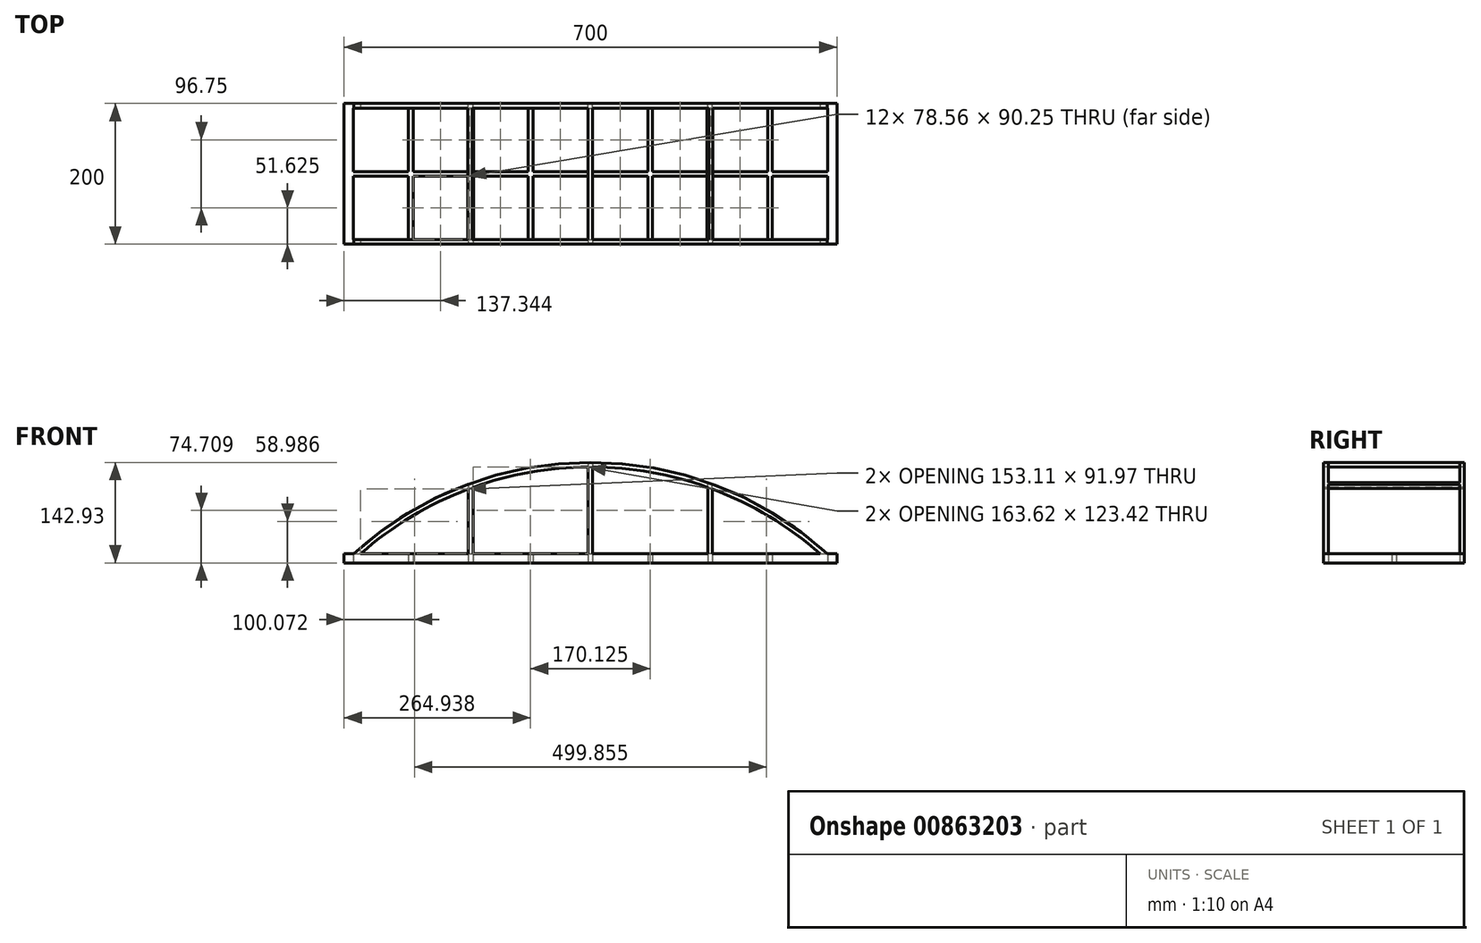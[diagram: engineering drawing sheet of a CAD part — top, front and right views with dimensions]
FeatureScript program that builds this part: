
annotation { "Feature Type Name" : "Feature", "Feature Type Description" : "" }
export const myFeature = defineFeature(function(context is Context, id is Id, definition is map)
    precondition{}
    {
        {
            var Q0;
            Q0=qCreatedBy(makeId("Top.planeOp"),FACE);
            var sketch = newSketch(context, id + "F0", { "sketchPlane" : qUnion([Q0])});
            skLineSegment(sketch, "E0.bottom", {"start": v(-350, 100) * mm, "end": v(350, 100) * mm});
            skLineSegment(sketch, "E0.top", {"start": v(-350, -100) * mm, "end": v(350, -100) * mm});
            skLineSegment(sketch, "E0.left", {"start": v(-350, 100) * mm, "end": v(-350, -100) * mm});
            skLineSegment(sketch, "E0.right", {"start": v(350, 100) * mm, "end": v(350, -100) * mm});
            skLineSegment(sketch, "E1.bottom", {"start": v(-337, 93.5) * mm, "end": v(337, 93.5) * mm});
            skLineSegment(sketch, "E1.top", {"start": v(-337, -93.5) * mm, "end": v(337, -93.5) * mm});
            skLineSegment(sketch, "E1.left", {"start": v(-337, 93.5) * mm, "end": v(-337, -93.5) * mm});
            skLineSegment(sketch, "E1.right", {"start": v(337, 93.5) * mm, "end": v(337, -93.5) * mm});
            skLineSegment(sketch, "E2.bottom", {"start": v(-337, 3.25) * mm, "end": v(337, 3.25) * mm});
            skLineSegment(sketch, "E2.top", {"start": v(-337, -3.25) * mm, "end": v(337, -3.25) * mm});
            skLineSegment(sketch, "E2.left", {"start": v(-337, 3.25) * mm, "end": v(-337, -3.25) * mm});
            skLineSegment(sketch, "E2.right", {"start": v(337, 3.25) * mm, "end": v(337, -3.25) * mm});
            skLineSegment(sketch, "E3.bottom", {"start": v(-258.44, 93.5) * mm, "end": v(-251.94, 93.5) * mm});
            skLineSegment(sketch, "E3.top", {"start": v(-258.44, -93.5) * mm, "end": v(-251.94, -93.5) * mm});
            skLineSegment(sketch, "E3.left", {"start": v(-258.44, 93.5) * mm, "end": v(-258.44, -93.5) * mm});
            skLineSegment(sketch, "E3.right", {"start": v(-251.94, 93.5) * mm, "end": v(-251.94, -93.5) * mm});
            skLineSegment(sketch, "E4.bottom", {"start": v(-173.38, 93.5) * mm, "end": v(-166.88, 93.5) * mm});
            skLineSegment(sketch, "E4.top", {"start": v(-173.37, -93.5) * mm, "end": v(-166.87, -93.5) * mm});
            skLineSegment(sketch, "E4.left", {"start": v(-173.38, 93.5) * mm, "end": v(-173.37, -93.5) * mm});
            skLineSegment(sketch, "E4.right", {"start": v(-166.88, 93.5) * mm, "end": v(-166.87, -93.5) * mm});
            skLineSegment(sketch, "E5.bottom", {"start": v(-88.31, 93.5) * mm, "end": v(-81.81, 93.5) * mm});
            skLineSegment(sketch, "E5.top", {"start": v(-88.31, -93.5) * mm, "end": v(-81.81, -93.5) * mm});
            skLineSegment(sketch, "E5.left", {"start": v(-88.31, 93.5) * mm, "end": v(-88.31, -93.5) * mm});
            skLineSegment(sketch, "E5.right", {"start": v(-81.81, 93.5) * mm, "end": v(-81.81, -93.5) * mm});
            skLineSegment(sketch, "E6.bottom", {"start": v(-3.25, 93.5) * mm, "end": v(3.25, 93.5) * mm});
            skLineSegment(sketch, "E6.top", {"start": v(-3.25, -93.5) * mm, "end": v(3.25, -93.5) * mm});
            skLineSegment(sketch, "E6.left", {"start": v(-3.25, 93.5) * mm, "end": v(-3.25, -93.5) * mm});
            skLineSegment(sketch, "E6.right", {"start": v(3.25, 93.5) * mm, "end": v(3.25, -93.5) * mm});
            skLineSegment(sketch, "E7.MirrorCS", {"start": v(81.81, 93.5) * mm, "end": v(81.81, -93.5) * mm});
            skLineSegment(sketch, "E8.MirrorCS", {"start": v(88.31, 93.5) * mm, "end": v(88.31, -93.5) * mm});
            skLineSegment(sketch, "E9.MirrorCS", {"start": v(166.88, 93.5) * mm, "end": v(166.87, -93.5) * mm});
            skLineSegment(sketch, "E10.MirrorCS", {"start": v(173.38, 93.5) * mm, "end": v(173.37, -93.5) * mm});
            skLineSegment(sketch, "E11.MirrorCS", {"start": v(251.94, 93.5) * mm, "end": v(251.94, -93.5) * mm});
            skLineSegment(sketch, "E12.MirrorCS", {"start": v(258.44, 93.5) * mm, "end": v(258.44, -93.5) * mm});
            skSolve(sketch);
        }
        {
            var Q0;
            Q0=makeQuery(id+"F0.imprint","IMPRINT",FACE,{"disambiguationData":[TD([[makeQuery(id+"F0.imprint","IMPRINT",EDGE,{"derivedFrom":sQuery(id+"F0.wireOp",EDGE,"E0.bottom")}),-1.0]])]});
            var Q1;
            {var subQ0=sQuery(id+"F0.wireOp",EDGE,"E11.MirrorCS");var subQ1=sQuery(id+"F0.wireOp",EDGE,"E2.bottom");var subQ2=makeQuery(id+"F0.imprint","INTERSECT",VERTEX,{"derivedFrom":[subQ1,subQ0]});var subQ3=sQuery(id+"F0.wireOp",EDGE,"E10.MirrorCS");var subQ4=makeQuery(id+"F0.imprint","INTERSECT",VERTEX,{"derivedFrom":[subQ1,subQ3]});var subQ5=sQuery(id+"F0.wireOp",EDGE,"E2.top");var subQ10=sQuery(id+"F0.wireOp",EDGE,"E12.MirrorCS");var subQ11=makeQuery(id+"F0.imprint","INTERSECT",VERTEX,{"derivedFrom":[subQ1,subQ10]});var subQ14=sQuery(id+"F0.wireOp",EDGE,"E5.left");var subQ15=makeQuery(id+"F0.imprint","INTERSECT",VERTEX,{"derivedFrom":[subQ1,subQ14]});var subQ16=sQuery(id+"F0.wireOp",EDGE,"E4.right");var subQ17=makeQuery(id+"F0.imprint","INTERSECT",VERTEX,{"derivedFrom":[subQ1,subQ16]});var subQ22=sQuery(id+"F0.wireOp",EDGE,"E9.MirrorCS");var subQ23=makeQuery(id+"F0.imprint","INTERSECT",VERTEX,{"derivedFrom":[subQ1,subQ22]});var subQ26=sQuery(id+"F0.wireOp",EDGE,"E5.right");var subQ27=makeQuery(id+"F0.imprint","INTERSECT",VERTEX,{"derivedFrom":[subQ1,subQ26]});var subQ28=sQuery(id+"F0.wireOp",EDGE,"E6.left");var subQ29=makeQuery(id+"F0.imprint","INTERSECT",VERTEX,{"derivedFrom":[subQ1,subQ28]});var subQ34=sQuery(id+"F0.wireOp",EDGE,"E8.MirrorCS");var subQ35=makeQuery(id+"F0.imprint","INTERSECT",VERTEX,{"derivedFrom":[subQ1,subQ34]});var subQ42=sQuery(id+"F0.wireOp",EDGE,"E1.right");var subQ43=makeQuery(id+"F0.imprint","INTERSECT",VERTEX,{"derivedFrom":[subQ42,subQ5]});var subQ45=sQuery(id+"F0.wireOp",EDGE,"E3.right");var subQ46=makeQuery(id+"F0.imprint","INTERSECT",VERTEX,{"derivedFrom":[subQ1,subQ45]});var subQ49=sQuery(id+"F0.wireOp",EDGE,"E7.MirrorCS");var subQ50=makeQuery(id+"F0.imprint","INTERSECT",VERTEX,{"derivedFrom":[subQ1,subQ49]});var subQ57=sQuery(id+"F0.wireOp",EDGE,"E1.left");var subQ58=makeQuery(id+"F0.imprint","INTERSECT",VERTEX,{"derivedFrom":[subQ57,subQ5]});Q1=qUnion([makeQuery(id+"F0.imprint","IMPRINT",FACE,{"disambiguationData":[TD([[makeQuery(id+"F0.imprint","IMPRINT",EDGE,{"disambiguationData":[TD([[subQ46,1.0]])],"derivedFrom":subQ1}),-1.0]])]}),makeQuery(id+"F0.imprint","IMPRINT",FACE,{"disambiguationData":[TD([[makeQuery(id+"F0.imprint","IMPRINT",EDGE,{"disambiguationData":[TD([[subQ29,-1.0]])],"derivedFrom":subQ1}),-1.0]])]}),makeQuery(id+"F0.imprint","IMPRINT",FACE,{"disambiguationData":[TD([[makeQuery(id+"F0.imprint","IMPRINT",EDGE,{"disambiguationData":[TD([[subQ58,1.0]])],"derivedFrom":subQ57}),1.0]])]}),makeQuery(id+"F0.imprint","IMPRINT",FACE,{"disambiguationData":[TD([[makeQuery(id+"F0.imprint","IMPRINT",EDGE,{"disambiguationData":[TD([[subQ50,1.0]])],"derivedFrom":subQ1}),-1.0]])]}),makeQuery(id+"F0.imprint","IMPRINT",FACE,{"disambiguationData":[TD([[makeQuery(id+"F0.imprint","IMPRINT",EDGE,{"disambiguationData":[TD([[subQ35,1.0]])],"derivedFrom":subQ1}),-1.0]])]}),makeQuery(id+"F0.imprint","IMPRINT",FACE,{"disambiguationData":[TD([[makeQuery(id+"F0.imprint","IMPRINT",EDGE,{"disambiguationData":[TD([[subQ46,-1.0]])],"derivedFrom":subQ1}),-1.0]])]}),makeQuery(id+"F0.imprint","IMPRINT",FACE,{"disambiguationData":[TD([[makeQuery(id+"F0.imprint","IMPRINT",EDGE,{"disambiguationData":[TD([[subQ43,1.0]])],"derivedFrom":subQ42}),-1.0]])]}),makeQuery(id+"F0.imprint","IMPRINT",FACE,{"disambiguationData":[TD([[makeQuery(id+"F0.imprint","IMPRINT",EDGE,{"disambiguationData":[TD([[subQ17,1.0]])],"derivedFrom":subQ1}),-1.0]])]}),makeQuery(id+"F0.imprint","IMPRINT",FACE,{"disambiguationData":[TD([[makeQuery(id+"F0.imprint","IMPRINT",EDGE,{"disambiguationData":[TD([[subQ23,1.0]])],"derivedFrom":subQ1}),-1.0]])]}),makeQuery(id+"F0.imprint","IMPRINT",FACE,{"disambiguationData":[TD([[makeQuery(id+"F0.imprint","IMPRINT",EDGE,{"disambiguationData":[TD([[subQ15,-1.0]])],"derivedFrom":subQ1}),-1.0]])]}),makeQuery(id+"F0.imprint","IMPRINT",FACE,{"disambiguationData":[TD([[makeQuery(id+"F0.imprint","IMPRINT",EDGE,{"disambiguationData":[TD([[subQ27,-1.0]])],"derivedFrom":subQ1}),-1.0]])]}),makeQuery(id+"F0.imprint","IMPRINT",FACE,{"disambiguationData":[TD([[makeQuery(id+"F0.imprint","IMPRINT",EDGE,{"disambiguationData":[TD([[subQ4,1.0]])],"derivedFrom":subQ1}),-1.0]])]}),makeQuery(id+"F0.imprint","IMPRINT",FACE,{"disambiguationData":[TD([[makeQuery(id+"F0.imprint","IMPRINT",EDGE,{"disambiguationData":[TD([[subQ15,1.0]])],"derivedFrom":subQ1}),-1.0]])]}),makeQuery(id+"F0.imprint","IMPRINT",FACE,{"disambiguationData":[TD([[makeQuery(id+"F0.imprint","IMPRINT",EDGE,{"disambiguationData":[TD([[subQ11,1.0]])],"derivedFrom":subQ1}),-1.0]])]}),makeQuery(id+"F0.imprint","IMPRINT",FACE,{"disambiguationData":[TD([[makeQuery(id+"F0.imprint","IMPRINT",EDGE,{"disambiguationData":[TD([[subQ2,1.0]])],"derivedFrom":subQ1}),-1.0]])]})]);}
            var Q2;
            {var subQ0=sQuery(id+"F0.wireOp",EDGE,"E3.right");var subQ1=sQuery(id+"F0.wireOp",EDGE,"E1.bottom");var subQ2=makeQuery(id+"F0.imprint","INTERSECT",VERTEX,{"derivedFrom":[subQ1,subQ0]});Q2=makeQuery(id+"F0.imprint","IMPRINT",FACE,{"disambiguationData":[TD([[makeQuery(id+"F0.imprint","IMPRINT",EDGE,{"disambiguationData":[TD([[subQ2,1.0]])],"derivedFrom":subQ1}),-1.0]])]});}
            var Q3;
            {var subQ0=sQuery(id+"F0.wireOp",EDGE,"E3.right");var subQ1=sQuery(id+"F0.wireOp",EDGE,"E1.top");var subQ2=makeQuery(id+"F0.imprint","INTERSECT",VERTEX,{"derivedFrom":[subQ1,subQ0]});Q3=makeQuery(id+"F0.imprint","IMPRINT",FACE,{"disambiguationData":[TD([[makeQuery(id+"F0.imprint","IMPRINT",EDGE,{"disambiguationData":[TD([[subQ2,1.0]])],"derivedFrom":subQ1}),1.0]])]});}
            var Q4;
            {var subQ0=sQuery(id+"F0.wireOp",EDGE,"E4.right");var subQ1=sQuery(id+"F0.wireOp",EDGE,"E1.bottom");var subQ2=makeQuery(id+"F0.imprint","INTERSECT",VERTEX,{"derivedFrom":[subQ1,subQ0]});Q4=makeQuery(id+"F0.imprint","IMPRINT",FACE,{"disambiguationData":[TD([[makeQuery(id+"F0.imprint","IMPRINT",EDGE,{"disambiguationData":[TD([[subQ2,1.0]])],"derivedFrom":subQ1}),-1.0]])]});}
            var Q5;
            {var subQ0=sQuery(id+"F0.wireOp",EDGE,"E4.left");var subQ1=sQuery(id+"F0.wireOp",EDGE,"E1.top");var subQ2=makeQuery(id+"F0.imprint","INTERSECT",VERTEX,{"derivedFrom":[subQ1,subQ0]});Q5=makeQuery(id+"F0.imprint","IMPRINT",FACE,{"disambiguationData":[TD([[makeQuery(id+"F0.imprint","IMPRINT",EDGE,{"disambiguationData":[TD([[subQ2,-1.0]])],"derivedFrom":subQ1}),1.0]])]});}
            var Q6;
            {var subQ0=sQuery(id+"F0.wireOp",EDGE,"E5.left");var subQ1=sQuery(id+"F0.wireOp",EDGE,"E1.bottom");var subQ2=makeQuery(id+"F0.imprint","INTERSECT",VERTEX,{"derivedFrom":[subQ1,subQ0]});Q6=makeQuery(id+"F0.imprint","IMPRINT",FACE,{"disambiguationData":[TD([[makeQuery(id+"F0.imprint","IMPRINT",EDGE,{"disambiguationData":[TD([[subQ2,-1.0]])],"derivedFrom":subQ1}),-1.0]])]});}
            var Q7;
            {var subQ0=sQuery(id+"F0.wireOp",EDGE,"E5.right");var subQ1=sQuery(id+"F0.wireOp",EDGE,"E1.top");var subQ2=makeQuery(id+"F0.imprint","INTERSECT",VERTEX,{"derivedFrom":[subQ1,subQ0]});Q7=makeQuery(id+"F0.imprint","IMPRINT",FACE,{"disambiguationData":[TD([[makeQuery(id+"F0.imprint","IMPRINT",EDGE,{"disambiguationData":[TD([[subQ2,1.0]])],"derivedFrom":subQ1}),1.0]])]});}
            var Q8;
            {var subQ0=sQuery(id+"F0.wireOp",EDGE,"E6.left");var subQ1=sQuery(id+"F0.wireOp",EDGE,"E1.bottom");var subQ2=makeQuery(id+"F0.imprint","INTERSECT",VERTEX,{"derivedFrom":[subQ1,subQ0]});Q8=makeQuery(id+"F0.imprint","IMPRINT",FACE,{"disambiguationData":[TD([[makeQuery(id+"F0.imprint","IMPRINT",EDGE,{"disambiguationData":[TD([[subQ2,-1.0]])],"derivedFrom":subQ1}),-1.0]])]});}
            var Q9;
            {var subQ0=sQuery(id+"F0.wireOp",EDGE,"E6.left");var subQ1=sQuery(id+"F0.wireOp",EDGE,"E1.top");var subQ2=makeQuery(id+"F0.imprint","INTERSECT",VERTEX,{"derivedFrom":[subQ1,subQ0]});Q9=makeQuery(id+"F0.imprint","IMPRINT",FACE,{"disambiguationData":[TD([[makeQuery(id+"F0.imprint","IMPRINT",EDGE,{"disambiguationData":[TD([[subQ2,-1.0]])],"derivedFrom":subQ1}),1.0]])]});}
            var Q10;
            {var subQ0=sQuery(id+"F0.wireOp",EDGE,"E8.MirrorCS");var subQ1=sQuery(id+"F0.wireOp",EDGE,"E1.bottom");var subQ2=makeQuery(id+"F0.imprint","INTERSECT",VERTEX,{"derivedFrom":[subQ1,subQ0]});Q10=makeQuery(id+"F0.imprint","IMPRINT",FACE,{"disambiguationData":[TD([[makeQuery(id+"F0.imprint","IMPRINT",EDGE,{"disambiguationData":[TD([[subQ2,1.0]])],"derivedFrom":subQ1}),-1.0]])]});}
            var Q11;
            {var subQ0=sQuery(id+"F0.wireOp",EDGE,"E8.MirrorCS");var subQ1=sQuery(id+"F0.wireOp",EDGE,"E1.top");var subQ2=makeQuery(id+"F0.imprint","INTERSECT",VERTEX,{"derivedFrom":[subQ1,subQ0]});Q11=makeQuery(id+"F0.imprint","IMPRINT",FACE,{"disambiguationData":[TD([[makeQuery(id+"F0.imprint","IMPRINT",EDGE,{"disambiguationData":[TD([[subQ2,1.0]])],"derivedFrom":subQ1}),1.0]])]});}
            var Q12;
            {var subQ0=sQuery(id+"F0.wireOp",EDGE,"E9.MirrorCS");var subQ1=sQuery(id+"F0.wireOp",EDGE,"E1.bottom");var subQ2=makeQuery(id+"F0.imprint","INTERSECT",VERTEX,{"derivedFrom":[subQ1,subQ0]});Q12=makeQuery(id+"F0.imprint","IMPRINT",FACE,{"disambiguationData":[TD([[makeQuery(id+"F0.imprint","IMPRINT",EDGE,{"disambiguationData":[TD([[subQ2,-1.0]])],"derivedFrom":subQ1}),-1.0]])]});}
            var Q13;
            {var subQ0=sQuery(id+"F0.wireOp",EDGE,"E10.MirrorCS");var subQ1=sQuery(id+"F0.wireOp",EDGE,"E1.top");var subQ2=makeQuery(id+"F0.imprint","INTERSECT",VERTEX,{"derivedFrom":[subQ1,subQ0]});Q13=makeQuery(id+"F0.imprint","IMPRINT",FACE,{"disambiguationData":[TD([[makeQuery(id+"F0.imprint","IMPRINT",EDGE,{"disambiguationData":[TD([[subQ2,1.0]])],"derivedFrom":subQ1}),1.0]])]});}
            var Q14;
            {var subQ0=sQuery(id+"F0.wireOp",EDGE,"E12.MirrorCS");var subQ1=sQuery(id+"F0.wireOp",EDGE,"E1.bottom");var subQ2=makeQuery(id+"F0.imprint","INTERSECT",VERTEX,{"derivedFrom":[subQ1,subQ0]});Q14=makeQuery(id+"F0.imprint","IMPRINT",FACE,{"disambiguationData":[TD([[makeQuery(id+"F0.imprint","IMPRINT",EDGE,{"disambiguationData":[TD([[subQ2,1.0]])],"derivedFrom":subQ1}),-1.0]])]});}
            var Q15;
            {var subQ0=sQuery(id+"F0.wireOp",EDGE,"E12.MirrorCS");var subQ1=sQuery(id+"F0.wireOp",EDGE,"E1.top");var subQ2=makeQuery(id+"F0.imprint","INTERSECT",VERTEX,{"derivedFrom":[subQ1,subQ0]});Q15=makeQuery(id+"F0.imprint","IMPRINT",FACE,{"disambiguationData":[TD([[makeQuery(id+"F0.imprint","IMPRINT",EDGE,{"disambiguationData":[TD([[subQ2,1.0]])],"derivedFrom":subQ1}),1.0]])]});}
            extrude(context, id + "F1", {"entities" : qUnion([Q0, Q1, Q2, Q3, Q4, Q5, Q6, Q7, Q8, Q9, Q10, Q11, Q12, Q13, Q14, Q15]), "depth" : 13 * mm, "offsetDistance" : 25 * mm});
        }
        {
            var Q0;
            Q0=makeQuery(id+"F1.opExtrude","SWEPT_FACE",FACE,{"disambiguationData":[OSD([sQuery(id+"F0.wireOp",EDGE,"E0.top")])]});
            var sketch = newSketch(context, id + "F2", { "sketchPlane" : qUnion([Q0])});
            skLineSegment(sketch, "E13", {"start": v(0, 0) * mm, "end": v(0, 13) * mm});
            skArc(sketch, "E14", {"start": v(350, 0) * mm, "mid": v(0, 142.93) * mm, "end": v(-350, 0) * mm});
            skArc(sketch, "E15", {"start": v(340.65, 0) * mm, "mid": v(0, 136.43) * mm, "end": v(-340.65, 0) * mm});
            skLineSegment(sketch, "E16", {"start": v(-350, 0) * mm, "end": v(-339.96, 0) * mm});
            skLineSegment(sketch, "E17", {"start": v(350, 0) * mm, "end": v(340.65, 0) * mm});
            skLineSegment(sketch, "E18", {"start": v(340.65, 0) * mm, "end": v(340.02, 0) * mm});
            skSolve(sketch);
        }
        {
            var Q0;
            {var subQ0=sQuery(id+"F2.wireOp",EDGE,"E14");var subQ1=makeQuery(id+"F1.opExtrude","CAP_EDGE",EDGE,{"disambiguationData":[OSD([sQuery(id+"F0.wireOp",EDGE,"E0.top")])],"isStart":false});var subQ2=makeQuery(id+"F2.imprint","INTERSECT",VERTEX,{"disambiguationData":[OD(0.0)],"derivedFrom":[subQ1,subQ0]});Q0=makeQuery(id+"F2.imprint","IMPRINT",FACE,{"disambiguationData":[TD([[makeQuery(id+"F2.imprint","IMPRINT",EDGE,{"disambiguationData":[TD([[subQ2,-1.0]])],"derivedFrom":subQ0}),1.0]])]});}
            extrude(context, id + "F3", {"entities" : qUnion([Q0]), "oppositeDirection" : true, "depth" : 200 * mm, "offsetDistance" : 25 * mm});
        }
        {
            var Q0;
            Q0=makeQuery(id+"F1.opExtrude","SWEPT_FACE",FACE,{"disambiguationData":[OSD([sQuery(id+"F0.wireOp",EDGE,"E0.left")])]});
            var sketch = newSketch(context, id + "F4", { "sketchPlane" : qUnion([Q0])});
            skLineSegment(sketch, "E19.bottom", {"start": v(-100, 13) * mm, "end": v(100, 13) * mm});
            skLineSegment(sketch, "E19.top", {"start": v(-100, 145) * mm, "end": v(100, 145) * mm});
            skLineSegment(sketch, "E19.left", {"start": v(-100, 13) * mm, "end": v(-100, 145) * mm});
            skLineSegment(sketch, "E19.right", {"start": v(100, 13) * mm, "end": v(100, 145) * mm});
            skLineSegment(sketch, "E20.bottom", {"start": v(-100, 13) * mm, "end": v(-93.5, 13) * mm});
            skLineSegment(sketch, "E20.top", {"start": v(-100, 145) * mm, "end": v(-93.5, 145) * mm});
            skLineSegment(sketch, "E20.right", {"start": v(-93.5, 13) * mm, "end": v(-93.5, 145) * mm});
            skLineSegment(sketch, "E21.MirrorCS", {"start": v(93.5, 13) * mm, "end": v(93.5, 145) * mm});
            skSolve(sketch);
        }
        {
            var Q0;
            {var subQ0=sQuery(id+"F4.wireOp",EDGE,"E20.right");Q0=makeQuery(id+"F4.imprint","IMPRINT",FACE,{"disambiguationData":[TD([[makeQuery(id+"F4.imprint","IMPRINT",EDGE,{"derivedFrom":subQ0}),-1.0]])]});}
            extrude(context, id + "F5", {"entities" : qUnion([Q0]), "operationType" : NewBodyOperationType.REMOVE, "oppositeDirection" : true, "depth" : 700 * mm, "offsetDistance" : 25 * mm});
        }
        {
            var Q0;
            Q0=makeQuery(id+"F5.boolean.opBoolean","COPY",FACE,{"derivedFrom":makeQuery(id+"F5.opExtrude","SWEPT_FACE",FACE,{"disambiguationData":[OSD([sQuery(id+"F4.wireOp",EDGE,"E20.right")])]})});
            var sketch = newSketch(context, id + "F6", { "sketchPlane" : qUnion([Q0])});
            skLineSegment(sketch, "E22", {"start": v(0, 136.43) * mm, "end": v(0, 0) * mm});
            skCircle(sketch, "E23", {"center": v(0, -357.07) * mm, "radius": 500 * mm});
            skCircle(sketch, "E24", {"center": v(0, -357.07) * mm, "radius": 493.5 * mm});
            skLineSegment(sketch, "E25.bottom", {"start": v(-3.25, 145.95) * mm, "end": v(3.25, 145.95) * mm});
            skLineSegment(sketch, "E25.top", {"start": v(-3.25, 131.44) * mm, "end": v(3.25, 131.44) * mm});
            skLineSegment(sketch, "E25.left", {"start": v(-3.25, 145.95) * mm, "end": v(-3.25, 131.44) * mm});
            skLineSegment(sketch, "E25.right", {"start": v(3.25, 145.95) * mm, "end": v(3.25, 131.44) * mm});
            skLineSegment(sketch, "E26", {"start": v(0, 14.61) * mm, "end": v(160, 13) * mm});
            skLineSegment(sketch, "E27", {"start": v(0, -357.07) * mm, "end": v(194.07, 176.13) * mm});
            skLineSegment(sketch, "E28", {"start": v(0, 0) * mm, "end": v(0, -357.07) * mm});
            skLineSegment(sketch, "E29", {"start": v(167.88, 104.17) * mm, "end": v(164.83, 105.29) * mm});
            skLineSegment(sketch, "E30", {"start": v(164.83, 105.29) * mm, "end": v(170.93, 103.06) * mm});
            skLineSegment(sketch, "E31", {"start": v(164.83, 105.29) * mm, "end": v(169.38, 117.81) * mm});
            skLineSegment(sketch, "E32", {"start": v(170.93, 103.06) * mm, "end": v(175.59, 115.85) * mm});
            skLineSegment(sketch, "E33", {"start": v(175.59, 115.85) * mm, "end": v(169.38, 117.81) * mm});
            skLineSegment(sketch, "E34.MirrorCS", {"start": v(-164.83, 105.29) * mm, "end": v(-169.38, 117.81) * mm});
            skLineSegment(sketch, "E35.MirrorCS", {"start": v(-175.59, 115.85) * mm, "end": v(-169.38, 117.81) * mm});
            skLineSegment(sketch, "E36.MirrorCS", {"start": v(-170.93, 103.06) * mm, "end": v(-175.59, 115.85) * mm});
            skLineSegment(sketch, "E37.MirrorCS", {"start": v(-164.83, 105.29) * mm, "end": v(-170.93, 103.06) * mm});
            skLineSegment(sketch, "E38.MirrorCS", {"start": v(0, -357.07) * mm, "end": v(-194.07, 176.13) * mm});
            skSolve(sketch);
        }
        {
            var Q0;
            {var subQ0=sQuery(id+"F6.wireOp",EDGE,"E36.MirrorCS");var subQ1=sQuery(id+"F6.wireOp",EDGE,"E23");var subQ2=makeQuery(id+"F6.imprint","INTERSECT",VERTEX,{"derivedFrom":[subQ1,subQ0]});var subQ3=sQuery(id+"F6.wireOp",EDGE,"E38.MirrorCS");var subQ4=makeQuery(id+"F6.imprint","INTERSECT",VERTEX,{"derivedFrom":[subQ1,subQ3]});Q0=makeQuery(id+"F6.imprint","IMPRINT",FACE,{"disambiguationData":[TD([[makeQuery(id+"F6.imprint","IMPRINT",EDGE,{"disambiguationData":[TD([[subQ2,-1.0],[subQ4,1.0]])],"derivedFrom":subQ1}),-1.0]])]});}
            var Q1;
            {var subQ0=sQuery(id+"F6.wireOp",EDGE,"E34.MirrorCS");var subQ1=sQuery(id+"F6.wireOp",EDGE,"E23");var subQ2=makeQuery(id+"F6.imprint","INTERSECT",VERTEX,{"derivedFrom":[subQ1,subQ0]});var subQ3=sQuery(id+"F6.wireOp",EDGE,"E38.MirrorCS");var subQ4=makeQuery(id+"F6.imprint","INTERSECT",VERTEX,{"derivedFrom":[subQ1,subQ3]});Q1=makeQuery(id+"F6.imprint","IMPRINT",FACE,{"disambiguationData":[TD([[makeQuery(id+"F6.imprint","IMPRINT",EDGE,{"disambiguationData":[TD([[subQ2,1.0],[subQ4,-1.0]])],"derivedFrom":subQ1}),-1.0]])]});}
            var Q2;
            {var subQ2=sQuery(id+"F6.wireOp",EDGE,"E25.left");var subQ4=sQuery(id+"F6.wireOp",EDGE,"E25.right");var subQ5=sQuery(id+"F6.wireOp",EDGE,"E23");var subQ6=makeQuery(id+"F6.imprint","INTERSECT",VERTEX,{"derivedFrom":[subQ5,subQ4]});var subQ7=makeQuery(id+"F6.imprint","INTERSECT",VERTEX,{"derivedFrom":[subQ5,subQ2]});Q2=makeQuery(id+"F6.imprint","IMPRINT",FACE,{"disambiguationData":[TD([[makeQuery(id+"F6.imprint","IMPRINT",EDGE,{"disambiguationData":[TD([[subQ6,1.0],[subQ7,-1.0]])],"derivedFrom":subQ5}),-1.0]])]});}
            var Q3;
            {var subQ0=sQuery(id+"F6.wireOp",EDGE,"E31");var subQ1=sQuery(id+"F6.wireOp",EDGE,"E23");var subQ2=makeQuery(id+"F6.imprint","INTERSECT",VERTEX,{"derivedFrom":[subQ1,subQ0]});var subQ3=sQuery(id+"F6.wireOp",EDGE,"E27");var subQ4=makeQuery(id+"F6.imprint","INTERSECT",VERTEX,{"derivedFrom":[subQ1,subQ3]});Q3=makeQuery(id+"F6.imprint","IMPRINT",FACE,{"disambiguationData":[TD([[makeQuery(id+"F6.imprint","IMPRINT",EDGE,{"disambiguationData":[TD([[subQ2,-1.0],[subQ4,1.0]])],"derivedFrom":subQ1}),-1.0]])]});}
            var Q4;
            {var subQ0=sQuery(id+"F6.wireOp",EDGE,"E32");var subQ1=sQuery(id+"F6.wireOp",EDGE,"E23");var subQ2=makeQuery(id+"F6.imprint","INTERSECT",VERTEX,{"derivedFrom":[subQ1,subQ0]});var subQ3=sQuery(id+"F6.wireOp",EDGE,"E27");var subQ4=makeQuery(id+"F6.imprint","INTERSECT",VERTEX,{"derivedFrom":[subQ1,subQ3]});Q4=makeQuery(id+"F6.imprint","IMPRINT",FACE,{"disambiguationData":[TD([[makeQuery(id+"F6.imprint","IMPRINT",EDGE,{"disambiguationData":[TD([[subQ2,1.0],[subQ4,-1.0]])],"derivedFrom":subQ1}),-1.0]])]});}
            extrude(context, id + "F7", {"entities" : qUnion([Q0, Q1, Q2, Q3, Q4]), "operationType" : NewBodyOperationType.ADD, "depth" : 187 * mm, "offsetDistance" : 25 * mm});
        }
        {
            var Q0;
            Q0=makeQuery(id+"F1.opExtrude","CAP_FACE",FACE,{"disambiguationData":[OSD([sQuery(id+"F0.wireOp",EDGE,"E0.bottom"),sQuery(id+"F0.wireOp",EDGE,"E0.top"),sQuery(id+"F0.wireOp",EDGE,"E0.left"),sQuery(id+"F0.wireOp",EDGE,"E0.right"),sQuery(id+"F0.wireOp",EDGE,"E1.bottom"),sQuery(id+"F0.wireOp",EDGE,"E1.top"),sQuery(id+"F0.wireOp",EDGE,"E1.left"),sQuery(id+"F0.wireOp",EDGE,"E1.right"),sQuery(id+"F0.wireOp",EDGE,"E2.bottom"),sQuery(id+"F0.wireOp",EDGE,"E2.top"),sQuery(id+"F0.wireOp",EDGE,"E3.left"),sQuery(id+"F0.wireOp",EDGE,"E3.right"),sQuery(id+"F0.wireOp",EDGE,"E4.left"),sQuery(id+"F0.wireOp",EDGE,"E4.right"),sQuery(id+"F0.wireOp",EDGE,"E5.left"),sQuery(id+"F0.wireOp",EDGE,"E5.right"),sQuery(id+"F0.wireOp",EDGE,"E6.left"),sQuery(id+"F0.wireOp",EDGE,"E6.right"),sQuery(id+"F0.wireOp",EDGE,"E7.MirrorCS"),sQuery(id+"F0.wireOp",EDGE,"E8.MirrorCS"),sQuery(id+"F0.wireOp",EDGE,"E9.MirrorCS"),sQuery(id+"F0.wireOp",EDGE,"E10.MirrorCS"),sQuery(id+"F0.wireOp",EDGE,"E11.MirrorCS"),sQuery(id+"F0.wireOp",EDGE,"E12.MirrorCS")])],"isStart":false});
            var sketch = newSketch(context, id + "F8", { "sketchPlane" : qUnion([Q0])});
            skPoint(sketch, "E39.oppositeSnap0", {"position": v(0, -100) * mm});
            skLineSegment(sketch, "E39.bottom", {"start": v(-3.25, -93.5) * mm, "end": v(3.25, -93.5) * mm});
            skLineSegment(sketch, "E39.top", {"start": v(-3.25, -100) * mm, "end": v(3.25, -100) * mm});
            skLineSegment(sketch, "E39.left", {"start": v(-3.25, -93.5) * mm, "end": v(-3.25, -100) * mm});
            skLineSegment(sketch, "E39.right", {"start": v(3.25, -93.5) * mm, "end": v(3.25, -100) * mm});
            skLineSegment(sketch, "E40.MirrorCS", {"start": v(-3.25, 93.5) * mm, "end": v(-3.25, 100) * mm});
            skLineSegment(sketch, "E41.MirrorCS", {"start": v(-3.25, 93.5) * mm, "end": v(3.25, 93.5) * mm});
            skLineSegment(sketch, "E42.MirrorCS", {"start": v(3.25, 93.5) * mm, "end": v(3.25, 100) * mm});
            skLineSegment(sketch, "E43.MirrorCS", {"start": v(-3.25, 100) * mm, "end": v(3.25, 100) * mm});
            skLineSegment(sketch, "E44.bottom", {"start": v(-173.37, -93.5) * mm, "end": v(-166.87, -93.5) * mm});
            skLineSegment(sketch, "E44.top", {"start": v(-173.37, -100) * mm, "end": v(-166.87, -100) * mm});
            skLineSegment(sketch, "E44.left", {"start": v(-173.37, -93.5) * mm, "end": v(-173.37, -100) * mm});
            skLineSegment(sketch, "E44.right", {"start": v(-166.87, -93.5) * mm, "end": v(-166.87, -100) * mm});
            skLineSegment(sketch, "E45.MirrorCS", {"start": v(-173.37, 93.5) * mm, "end": v(-173.37, 100) * mm});
            skLineSegment(sketch, "E46.MirrorCS", {"start": v(-173.37, 93.5) * mm, "end": v(-166.87, 93.5) * mm});
            skLineSegment(sketch, "E47.MirrorCS", {"start": v(-166.87, 93.5) * mm, "end": v(-166.87, 100) * mm});
            skLineSegment(sketch, "E48.MirrorCS", {"start": v(-173.37, 100) * mm, "end": v(-166.87, 100) * mm});
            skLineSegment(sketch, "E49.MirrorCS", {"start": v(173.37, 93.5) * mm, "end": v(166.87, 93.5) * mm});
            skLineSegment(sketch, "E50.MirrorCS", {"start": v(173.37, 93.5) * mm, "end": v(173.37, 100) * mm});
            skLineSegment(sketch, "E51.MirrorCS", {"start": v(166.87, 93.5) * mm, "end": v(166.87, 100) * mm});
            skLineSegment(sketch, "E52.MirrorCS", {"start": v(173.37, 100) * mm, "end": v(166.87, 100) * mm});
            skLineSegment(sketch, "E53.MirrorCS", {"start": v(173.37, -93.5) * mm, "end": v(166.87, -93.5) * mm});
            skLineSegment(sketch, "E54.MirrorCS", {"start": v(173.37, -93.5) * mm, "end": v(173.37, -100) * mm});
            skLineSegment(sketch, "E55.MirrorCS", {"start": v(166.87, -93.5) * mm, "end": v(166.87, -100) * mm});
            skLineSegment(sketch, "E56.MirrorCS", {"start": v(173.37, -100) * mm, "end": v(166.87, -100) * mm});
            skSolve(sketch);
        }
        {
            var Q0;
            Q0=makeQuery(id+"F8.imprint","IMPRINT",FACE,{"disambiguationData":[TD([[makeQuery(id+"F8.imprint","IMPRINT",EDGE,{"derivedFrom":sQuery(id+"F8.wireOp",EDGE,"E39.bottom")}),-1.0]])]});
            var Q1;
            Q1=makeQuery(id+"F8.imprint","IMPRINT",FACE,{"disambiguationData":[TD([[makeQuery(id+"F8.imprint","IMPRINT",EDGE,{"derivedFrom":sQuery(id+"F8.wireOp",EDGE,"E40.MirrorCS")}),-1.0]])]});
            var Q2;
            Q2=makeQuery(id+"F8.imprint","IMPRINT",FACE,{"disambiguationData":[TD([[makeQuery(id+"F8.imprint","IMPRINT",EDGE,{"derivedFrom":sQuery(id+"F8.wireOp",EDGE,"E53.MirrorCS")}),1.0]])]});
            var Q3;
            Q3=makeQuery(id+"F8.imprint","IMPRINT",FACE,{"disambiguationData":[TD([[makeQuery(id+"F8.imprint","IMPRINT",EDGE,{"derivedFrom":sQuery(id+"F8.wireOp",EDGE,"E49.MirrorCS")}),-1.0]])]});
            var Q4;
            Q4=makeQuery(id+"F8.imprint","IMPRINT",FACE,{"disambiguationData":[TD([[makeQuery(id+"F8.imprint","IMPRINT",EDGE,{"derivedFrom":sQuery(id+"F8.wireOp",EDGE,"E45.MirrorCS")}),-1.0]])]});
            var Q5;
            Q5=makeQuery(id+"F8.imprint","IMPRINT",FACE,{"disambiguationData":[TD([[makeQuery(id+"F8.imprint","IMPRINT",EDGE,{"derivedFrom":sQuery(id+"F8.wireOp",EDGE,"E44.bottom")}),-1.0]])]});
            var Q6;
            Q6=makeQuery(id+"F5.boolean.opBoolean","SPLIT",BODY,{"disambiguationData":[OD(0.0)],"derivedFrom":makeQuery(id+"F3.opExtrude","SWEPT_BODY",BODY,{"disambiguationData":[OSD([sQuery(id+"F0.wireOp",EDGE,"E0.top"),sQuery(id+"F2.wireOp",EDGE,"E14"),sQuery(id+"F2.wireOp",EDGE,"E15")])]})});
            extrude(context, id + "F9", {"entities" : qUnion([Q0, Q1, Q2, Q3, Q4, Q5]), "operationType" : NewBodyOperationType.ADD, "endBound" : BoundingType.UP_TO_BODY, "depth" : 25 * mm, "endBoundEntityBody" : qUnion([Q6]), "offsetDistance" : 25 * mm});
        }
    });
